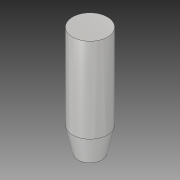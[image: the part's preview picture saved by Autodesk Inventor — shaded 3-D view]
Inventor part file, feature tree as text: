
AUTODESK INVENTOR PART (.ipt)
format: ipt  version: 2018 (Build 220112000, 112)  size: 86,016 bytes
history: native  units: in
note: dims shown in document units (in); Inventor stores cm internally (conversion verified against a paired STEP export)
features: chamfer x1
ambient origin geometry x8: Origin, YZ Plane, XZ Plane, XY Plane, X Axis, Y Axis, Z Axis, Center Point
bodies: Solid1 (feature_tree)
feature tree (1):
  chamfer  "Chamfer1"  [1 undecoded]
note: 1 required parameter value undecoded (feature->parameter linkage not recoverable at this tier; creation-order binding heuristic only, values carry confidence <= 0.55)
